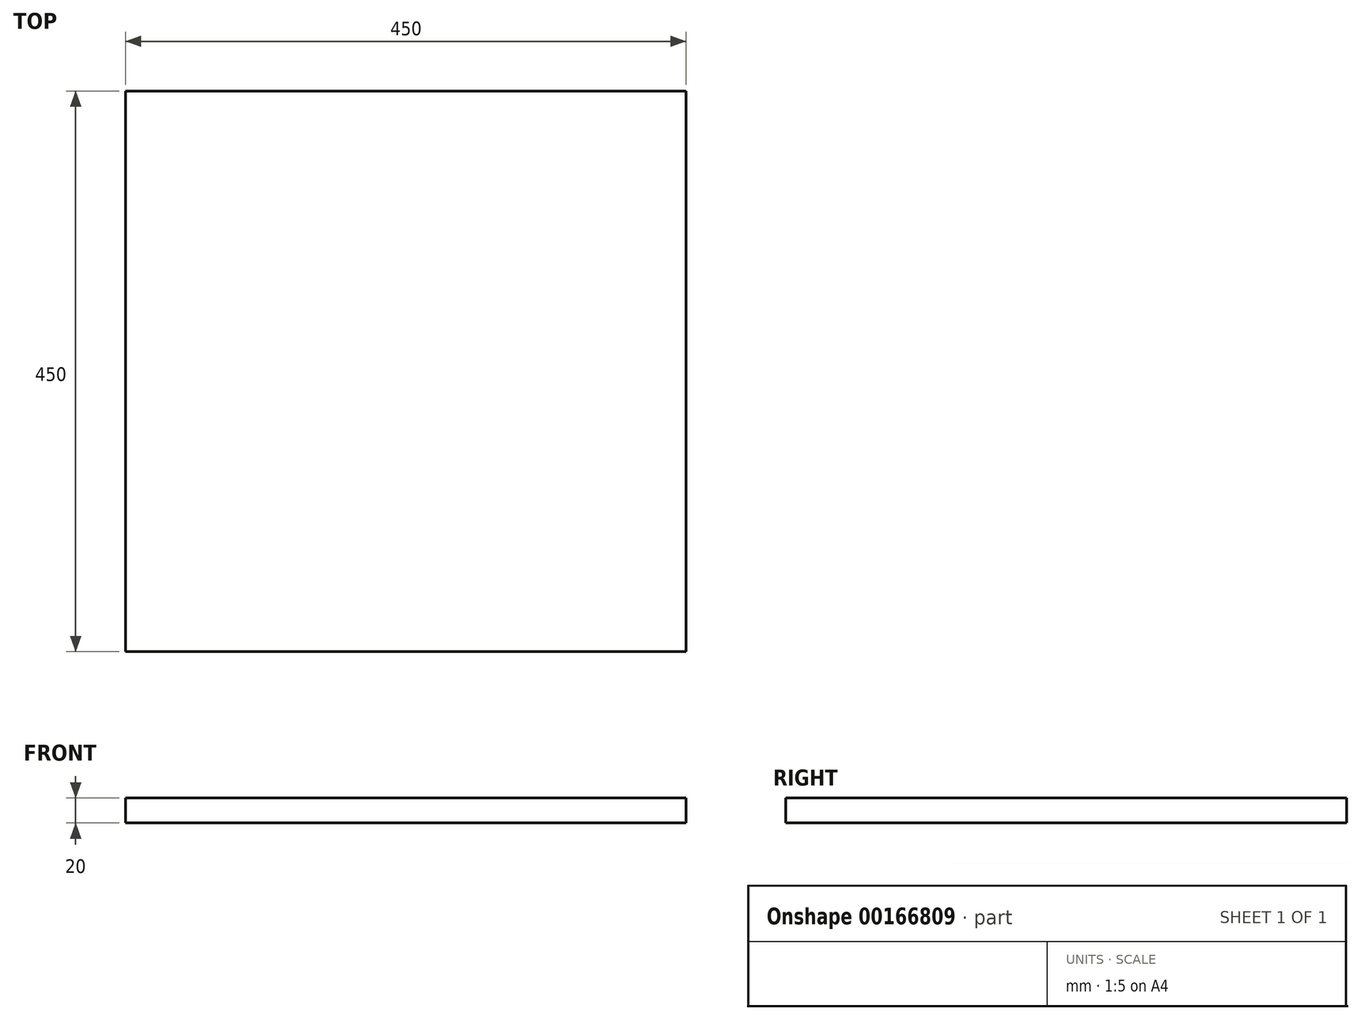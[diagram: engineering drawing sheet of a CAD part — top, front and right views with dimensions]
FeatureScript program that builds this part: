
annotation { "Feature Type Name" : "Feature", "Feature Type Description" : "" }
export const myFeature = defineFeature(function(context is Context, id is Id, definition is map)
    precondition{}
    {
        {
            var Q0;
            Q0=qCreatedBy(makeId("Top.planeOp"),FACE);
            var sketch = newSketch(context, id + "F0", { "sketchPlane" : qUnion([Q0])});
            skLineSegment(sketch, "E0.bottom", {"start": v(0, 0) * mm, "end": v(450, 0) * mm});
            skLineSegment(sketch, "E0.top", {"start": v(0, 450) * mm, "end": v(450, 450) * mm});
            skLineSegment(sketch, "E0.left", {"start": v(0, 0) * mm, "end": v(0, 450) * mm});
            skLineSegment(sketch, "E0.right", {"start": v(450, 0) * mm, "end": v(450, 450) * mm});
            skSolve(sketch);
        }
        {
            var Q0;
            Q0 = qSketchRegion(id + "F0", true);
            extrude(context, id + "F1", {"entities" : qUnion([Q0]), "depth" : 20 * mm});
        }
    });
